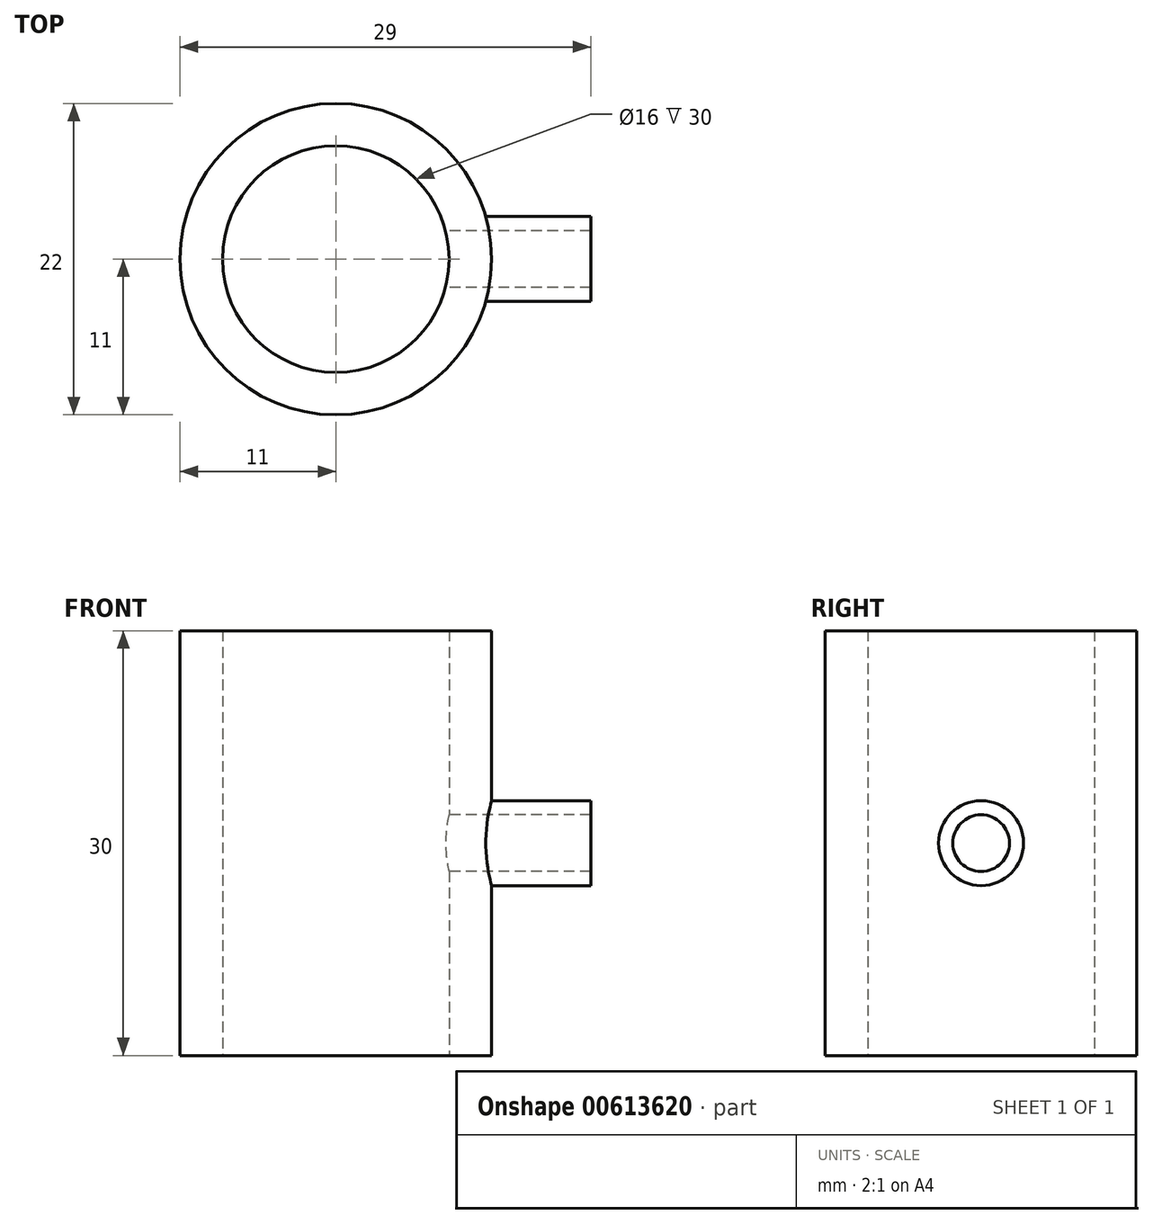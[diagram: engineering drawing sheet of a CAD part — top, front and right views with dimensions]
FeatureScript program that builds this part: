
annotation { "Feature Type Name" : "Feature", "Feature Type Description" : "" }
export const myFeature = defineFeature(function(context is Context, id is Id, definition is map)
    precondition{}
    {
        {
            var Q0;
            Q0=qCreatedBy(makeId("Top.planeOp"),FACE);
            var sketch = newSketch(context, id + "F0", { "sketchPlane" : qUnion([Q0])});
            skCircle(sketch, "E0", {"center": v(0, 0) * mm, "radius": 8 * mm});
            skCircle(sketch, "E1", {"center": v(0, 0) * mm, "radius": 11 * mm});
            skSolve(sketch);
        }
        {
            var Q0;
            Q0 = qSketchRegion(id + "F0", true);
            extrude(context, id + "F1", {"entities" : qUnion([Q0]), "depth" : 15 * mm, "offsetDistance" : 25 * mm, "hasSecondDirection" : true, "secondDirectionOppositeDirection" : true, "secondDirectionDepth" : 15 * mm});
        }
        {
            var Q0;
            Q0=qCreatedBy(makeId("Right.planeOp"),FACE);
            var sketch = newSketch(context, id + "F2", { "sketchPlane" : qUnion([Q0])});
            skCircle(sketch, "E2", {"center": v(0, 0) * mm, "radius": 2 * mm});
            skCircle(sketch, "E3", {"center": v(0, 0) * mm, "radius": 3 * mm});
            skSolve(sketch);
        }
        {
            var Q0;
            Q0=qCreatedBy(makeId("Right.planeOp"),FACE);
            cPlane(context, id + "F3", {"entities" : qUnion([Q0]), "cplaneType" : CPlaneType.OFFSET, "offset" : 8 * mm, "width" : 150 * mm, "height" : 150 * mm});
        }
        {
            var Q0;
            Q0=qCreatedBy(id+"F3.planeOp",FACE);
            var sketch = newSketch(context, id + "F4", { "sketchPlane" : qUnion([Q0])});
            skCircle(sketch, "E4.0", {"center": v(0, 0) * mm, "radius": 2 * mm});
            skCircle(sketch, "E5.0", {"center": v(0, 0) * mm, "radius": 3 * mm});
            skSolve(sketch);
        }
        {
            var Q0;
            Q0 = qSketchRegion(id + "F4", true);
            extrude(context, id + "F5", {"entities" : qUnion([Q0]), "operationType" : NewBodyOperationType.ADD, "depth" : 10 * mm, "offsetDistance" : 25 * mm});
        }
        {
            var Q0;
            Q0=sQuery(id+"F2.wireOp",VERTEX,"E3.center");
            var Q1;
            Q1=makeQuery(id+"F1.opExtrude","SWEPT_BODY",BODY,{"disambiguationData":[OSD([sQuery(id+"F0.wireOp",EDGE,"E0"),sQuery(id+"F0.wireOp",EDGE,"E1")])]});
            hole(context, id + "F6", {"style" : HoleStyle.SIMPLE, "endStyle" : HoleEndStyle.THROUGH, "oppositeDirection" : true, "holeDiameter" : 4 * mm, "majorDiameter" : 5 * mm, "isTappedThrough" : true, "tappedDepth" : 12 * mm, "tapClearance" : 3, "locations" : qUnion([Q0]), "scope" : qUnion([Q1])});
        }
    });
